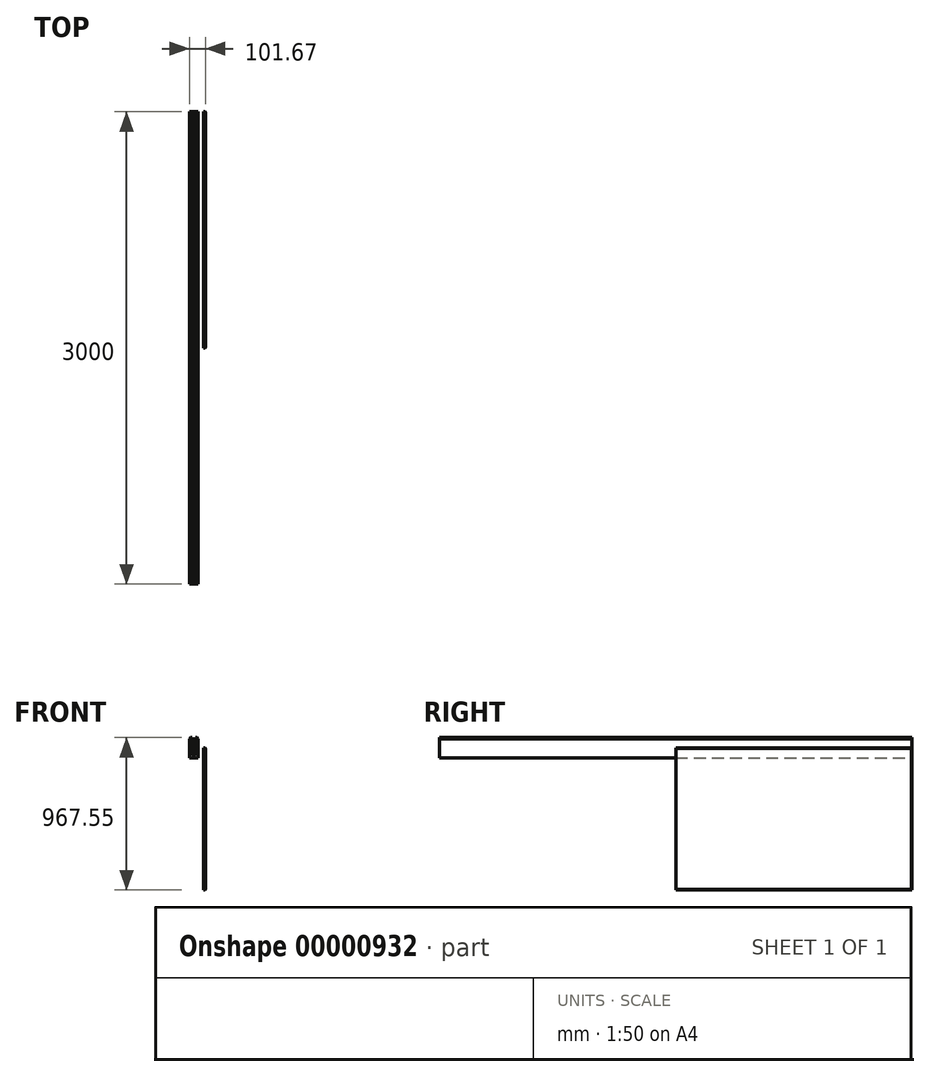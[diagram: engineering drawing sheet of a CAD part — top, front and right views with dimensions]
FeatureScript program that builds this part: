
annotation { "Feature Type Name" : "Feature", "Feature Type Description" : "" }
export const myFeature = defineFeature(function(context is Context, id is Id, definition is map)
    precondition{}
    {
        {
            var Q0;
            Q0=qCreatedBy(makeId("Front.planeOp"),FACE);
            var sketch = newSketch(context, id + "F0", { "sketchPlane" : qUnion([Q0])});
            skLineSegment(sketch, "E0", {"start": v(0, 0) * mm, "end": v(-55, 0) * mm});
            skLineSegment(sketch, "E1", {"start": v(-55, 0) * mm, "end": v(-55, 122) * mm});
            skLineSegment(sketch, "E2", {"start": v(-55, 122) * mm, "end": v(-47, 130) * mm});
            skLineSegment(sketch, "E3", {"start": v(-47, 130) * mm, "end": v(-40, 130) * mm});
            skLineSegment(sketch, "E4", {"start": v(-40, 130) * mm, "end": v(-40, 15) * mm});
            skLineSegment(sketch, "E5", {"start": v(-40, 15) * mm, "end": v(-15, 15) * mm});
            skLineSegment(sketch, "E6", {"start": v(-15, 15) * mm, "end": v(-15, 130) * mm});
            skLineSegment(sketch, "E7", {"start": v(-15, 130) * mm, "end": v(-8, 130) * mm});
            skLineSegment(sketch, "E8", {"start": v(-8, 130) * mm, "end": v(0, 122) * mm});
            skLineSegment(sketch, "E9", {"start": v(0, 122) * mm, "end": v(0, 0) * mm});
            skLineSegment(sketch, "E10", {"start": v(-27.5, 15) * mm, "end": v(-27.5, 0) * mm, "construction": true});
            skArc(sketch, "E11", {"start": v(0, 0) * mm, "mid": v(-27.5, 2.24) * mm, "end": v(-55, 0) * mm});
            skSolve(sketch);
        }
        {
            var Q0;
            {Q0=qUnion([makeQuery(id+"F0.imprint","IMPRINT",FACE,{"disambiguationData":[TD([[makeQuery(id+"F0.imprint","IMPRINT",EDGE,{"derivedFrom":sQuery(id+"F0.wireOp",EDGE,"E0")}),-1.0]])]}),makeQuery(id+"F0.imprint","IMPRINT",FACE,{"disambiguationData":[TD([[makeQuery(id+"F0.imprint","IMPRINT",EDGE,{"derivedFrom":sQuery(id+"F0.wireOp",EDGE,"E1")}),-1.0]])]})]);}
            extrude(context, id + "F1", {"entities" : qUnion([Q0]), "depth" : 3000 * mm});
        }
        {
            var Q0;
            Q0=qCreatedBy(makeId("Front.planeOp"),FACE);
            var sketch = newSketch(context, id + "F2", { "sketchPlane" : qUnion([Q0])});
            skLineSegment(sketch, "E12.bottom", {"start": v(33.91, 62.45) * mm, "end": v(46.67, 62.45) * mm});
            skLineSegment(sketch, "E12.top", {"start": v(33.91, -837.55) * mm, "end": v(46.67, -837.55) * mm});
            skLineSegment(sketch, "E12.left", {"start": v(33.91, 62.45) * mm, "end": v(33.91, -837.55) * mm});
            skLineSegment(sketch, "E12.right", {"start": v(46.67, 62.45) * mm, "end": v(46.67, -837.55) * mm});
            skSolve(sketch);
        }
        {
            var Q0;
            Q0=makeQuery(id+"F2.imprint","IMPRINT",FACE,{"disambiguationData":[TD([[makeQuery(id+"F2.imprint","IMPRINT",EDGE,{"derivedFrom":sQuery(id+"F2.wireOp",EDGE,"E12.bottom")}),-1.0]])]});
            extrude(context, id + "F3", {"entities" : qUnion([Q0]), "depth" : 1500 * mm});
        }
        {
            var Q0;
            Q0=makeQuery(id+"F3.opExtrude","SWEPT_FACE",FACE,{"disambiguationData":[OSD([sQuery(id+"F2.wireOp",EDGE,"E12.right")])]});
            chamfer(context, id + "F4", {"entities" : qUnion([Q0]), "width" : 2 * mm, "tangentPropagation" : true});
        }
        {
            var Q0;
            Q0=makeQuery(id+"F3.opExtrude","SWEPT_FACE",FACE,{"disambiguationData":[OSD([sQuery(id+"F2.wireOp",EDGE,"E12.left")])]});
            chamfer(context, id + "F5", {"entities" : qUnion([Q0]), "width" : 2 * mm, "tangentPropagation" : true});
        }
    });
